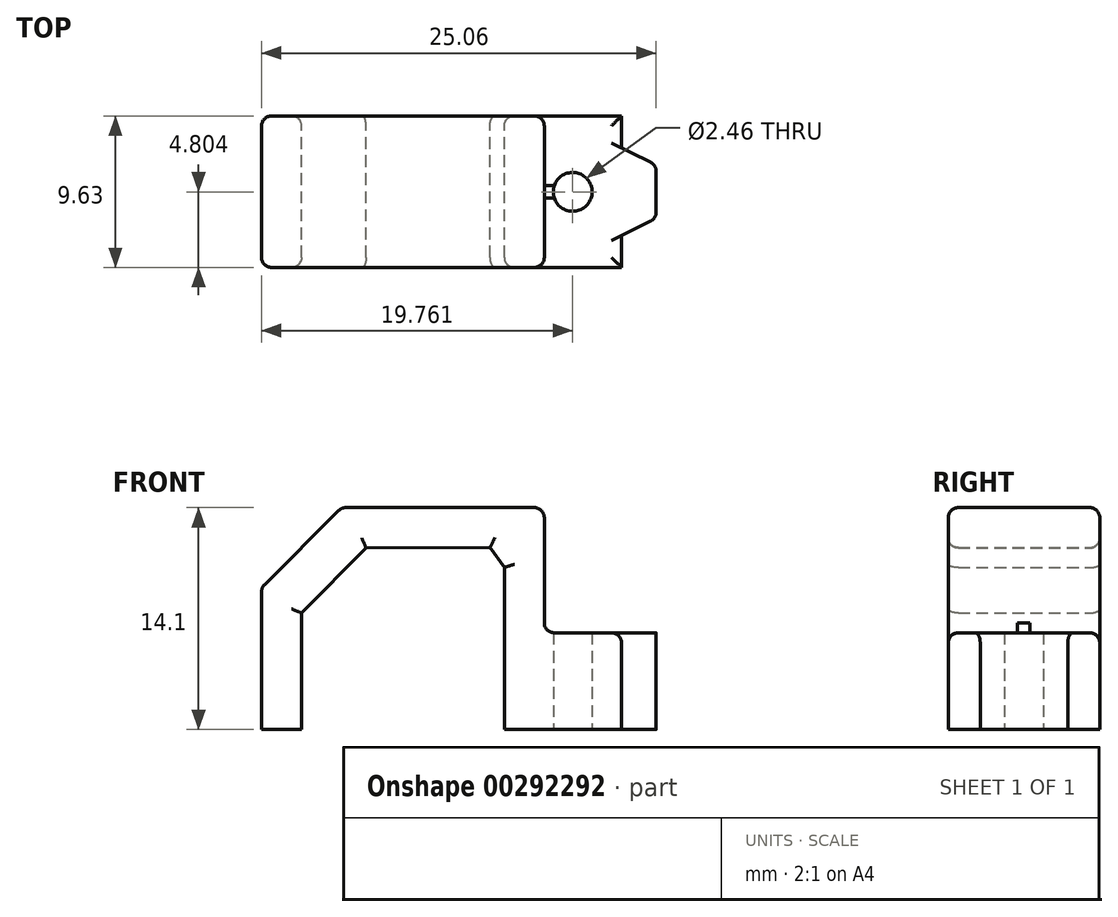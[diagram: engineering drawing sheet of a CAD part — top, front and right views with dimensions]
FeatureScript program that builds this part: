
annotation { "Feature Type Name" : "Feature", "Feature Type Description" : "" }
export const myFeature = defineFeature(function(context is Context, id is Id, definition is map)
    precondition{}
    {
        {
            var Q0;
            Q0=qCreatedBy(makeId("Front.planeOp"),FACE);
            var sketch = newSketch(context, id + "F0", { "sketchPlane" : qUnion([Q0])});
            skLineSegment(sketch, "E0", {"start": v(0, 0) * mm, "end": v(0, 6.14) * mm});
            skLineSegment(sketch, "E1", {"start": v(0, 6.14) * mm, "end": v(-4.9, 6.14) * mm});
            skLineSegment(sketch, "E2", {"start": v(-4.9, 6.14) * mm, "end": v(-4.9, 14.1) * mm});
            skLineSegment(sketch, "E3", {"start": v(-22.86, 0) * mm, "end": v(-20.32, 0) * mm});
            skLineSegment(sketch, "E4", {"start": v(-20.32, 0) * mm, "end": v(-20.32, 7.4) * mm});
            skLineSegment(sketch, "E5", {"start": v(-16.22, 11.53) * mm, "end": v(-8.35, 11.56) * mm});
            skLineSegment(sketch, "E6", {"start": v(-7.44, 10.3) * mm, "end": v(-7.44, 0) * mm});
            skLineSegment(sketch, "E7", {"start": v(-7.44, 0) * mm, "end": v(0, 0) * mm});
            skLineSegment(sketch, "E8", {"start": v(-7.44, 10.3) * mm, "end": v(-8.35, 11.56) * mm});
            skLineSegment(sketch, "E9", {"start": v(-17.78, 14.1) * mm, "end": v(-22.86, 9.02) * mm});
            skLineSegment(sketch, "E10", {"start": v(-16.22, 11.53) * mm, "end": v(-20.32, 7.4) * mm});
            skLineSegment(sketch, "E11", {"start": v(-22.86, 9.02) * mm, "end": v(-22.86, 0) * mm});
            skLineSegment(sketch, "E12", {"start": v(-17.78, 14.1) * mm, "end": v(-4.9, 14.1) * mm});
            skSolve(sketch);
        }
        {
            var Q0;
            Q0 = qSketchRegion(id + "F0", true);
            extrude(context, id + "F1", {"entities" : qUnion([Q0]), "depth" : 9.63 * mm});
        }
        {
            var Q0;
            Q0=makeQuery(id+"F1.opExtrude","SWEPT_FACE",FACE,{"disambiguationData":[OSD([sQuery(id+"F0.wireOp",EDGE,"E7")])]});
            var sketch = newSketch(context, id + "F2", { "sketchPlane" : qUnion([Q0])});
            skCircle(sketch, "E13", {"center": v(-3.1, 4.83) * mm, "radius": 1.17 * mm});
            skSolve(sketch);
        }
        {
            var Q0;
            Q0=sQuery(id+"F2.wireOp",VERTEX,"E13.center");
            var Q1;
            Q1=makeQuery(id+"F1.opExtrude","SWEPT_BODY",BODY,{"disambiguationData":[OSD([sQuery(id+"F0.wireOp",EDGE,"E0"),sQuery(id+"F0.wireOp",EDGE,"E1"),sQuery(id+"F0.wireOp",EDGE,"E2"),sQuery(id+"F0.wireOp",EDGE,"v06fyoa2-H6hD-baKa-V2WD-RjBCcUJbtUPS"),sQuery(id+"F0.wireOp",EDGE,"YEdOTz9l-d9wv-5XqQ-HbdA-mJVCXZZWVET7"),sQuery(id+"F0.wireOp",EDGE,"E3"),sQuery(id+"F0.wireOp",EDGE,"E4"),sQuery(id+"F0.wireOp",EDGE,"pneGorh0-Tr08-eoOQ-M8Zm-cxjPOqV0gIkG"),sQuery(id+"F0.wireOp",EDGE,"E5"),sQuery(id+"F0.wireOp",EDGE,"E6"),sQuery(id+"F0.wireOp",EDGE,"E7"),sQuery(id+"F0.wireOp",EDGE,"E8")])]});
            hole(context, id + "F3", {"style" : HoleStyle.SIMPLE, "endStyle" : HoleEndStyle.THROUGH, "holeDiameter" : 2.46 * mm, "tappedDepth" : 12.7 * mm, "tapClearance" : 3, "locations" : qUnion([Q0]), "scope" : qUnion([Q1])});
        }
        {
            var Q0;
            Q0=qCreatedBy(makeId("Top.planeOp"),FACE);
            var sketch = newSketch(context, id + "F4", { "sketchPlane" : qUnion([Q0])});
            skLineSegment(sketch, "E14", {"start": v(0, -7.6) * mm, "end": v(2.2, -6.5) * mm});
            skLineSegment(sketch, "E15", {"start": v(2.2, -3.12) * mm, "end": v(0, -2.03) * mm});
            skLineSegment(sketch, "E16", {"start": v(2.2, -6.5) * mm, "end": v(2.2, -3.12) * mm});
            skLineSegment(sketch, "E17", {"start": v(0, -7.6) * mm, "end": v(0, -2.03) * mm});
            skSolve(sketch);
        }
        {
            var Q0;
            Q0=makeQuery(id+"F4.imprint","IMPRINT",FACE,{"disambiguationData":[TD([[makeQuery(id+"F4.imprint","IMPRINT",EDGE,{"derivedFrom":sQuery(id+"F4.wireOp",EDGE,"E14")}),1.0]])]});
            var Q1;
            Q1=makeQuery(id+"F1.opExtrude","SWEPT_FACE",FACE,{"disambiguationData":[OSD([sQuery(id+"F0.wireOp",EDGE,"E1")])]});
            extrude(context, id + "F5", {"entities" : qUnion([Q0]), "operationType" : NewBodyOperationType.ADD, "endBound" : BoundingType.UP_TO_SURFACE, "endBoundEntityFace" : qUnion([Q1]), "depth" : 6.22 * mm});
        }
        {
            var Q0;
            Q0=makeQuery(id+"F1.opExtrude","CAP_EDGE",EDGE,{"disambiguationData":[OSD([sQuery(id+"F0.wireOp",EDGE,"v06fyoa2-H6hD-baKa-V2WD-RjBCcUJbtUPS")])],"isStart":true});
            var Q1;
            Q1=makeQuery(id+"F1.opExtrude","SWEPT_EDGE",EDGE,{"disambiguationData":[OSD([sQuery(id+"F0.wireOp",EDGE,"v06fyoa2-H6hD-baKa-V2WD-RjBCcUJbtUPS"),sQuery(id+"F0.wireOp",EDGE,"YEdOTz9l-d9wv-5XqQ-HbdA-mJVCXZZWVET7")])]});
            var Q2;
            Q2=makeQuery(id+"F1.opExtrude","CAP_EDGE",EDGE,{"disambiguationData":[OSD([sQuery(id+"F0.wireOp",EDGE,"v06fyoa2-H6hD-baKa-V2WD-RjBCcUJbtUPS")])],"isStart":false});
            var Q3;
            Q3=makeQuery(id+"F1.opExtrude","SWEPT_EDGE",EDGE,{"disambiguationData":[OSD([sQuery(id+"F0.wireOp",EDGE,"E2"),sQuery(id+"F0.wireOp",EDGE,"v06fyoa2-H6hD-baKa-V2WD-RjBCcUJbtUPS")])]});
            var Q4;
            Q4=makeQuery(id+"F1.opExtrude","CAP_EDGE",EDGE,{"disambiguationData":[OSD([sQuery(id+"F0.wireOp",EDGE,"E6")])],"isStart":true});
            var Q5;
            Q5=makeQuery(id+"F1.opExtrude","CAP_EDGE",EDGE,{"disambiguationData":[OSD([sQuery(id+"F0.wireOp",EDGE,"E8")])],"isStart":true});
            var Q6;
            Q6=makeQuery(id+"F1.opExtrude","CAP_EDGE",EDGE,{"disambiguationData":[OSD([sQuery(id+"F0.wireOp",EDGE,"E5")])],"isStart":true});
            var Q7;
            Q7=makeQuery(id+"F1.opExtrude","CAP_EDGE",EDGE,{"disambiguationData":[OSD([sQuery(id+"F0.wireOp",EDGE,"pneGorh0-Tr08-eoOQ-M8Zm-cxjPOqV0gIkG")])],"isStart":true});
            var Q8;
            Q8=makeQuery(id+"F1.opExtrude","CAP_EDGE",EDGE,{"disambiguationData":[OSD([sQuery(id+"F0.wireOp",EDGE,"E4")])],"isStart":true});
            var Q9;
            Q9=makeQuery(id+"F1.opExtrude","CAP_EDGE",EDGE,{"disambiguationData":[OSD([sQuery(id+"F0.wireOp",EDGE,"YEdOTz9l-d9wv-5XqQ-HbdA-mJVCXZZWVET7")])],"isStart":true});
            var Q10;
            Q10=makeQuery(id+"F1.opExtrude","CAP_EDGE",EDGE,{"disambiguationData":[OSD([sQuery(id+"F0.wireOp",EDGE,"YEdOTz9l-d9wv-5XqQ-HbdA-mJVCXZZWVET7")])],"isStart":false});
            var Q11;
            Q11=makeQuery(id+"F1.opExtrude","CAP_EDGE",EDGE,{"disambiguationData":[OSD([sQuery(id+"F0.wireOp",EDGE,"E4")])],"isStart":false});
            var Q12;
            Q12=makeQuery(id+"F1.opExtrude","CAP_EDGE",EDGE,{"disambiguationData":[OSD([sQuery(id+"F0.wireOp",EDGE,"pneGorh0-Tr08-eoOQ-M8Zm-cxjPOqV0gIkG")])],"isStart":false});
            var Q13;
            Q13=makeQuery(id+"F1.opExtrude","CAP_EDGE",EDGE,{"disambiguationData":[OSD([sQuery(id+"F0.wireOp",EDGE,"E5")])],"isStart":false});
            var Q14;
            Q14=makeQuery(id+"F1.opExtrude","CAP_EDGE",EDGE,{"disambiguationData":[OSD([sQuery(id+"F0.wireOp",EDGE,"E8")])],"isStart":false});
            var Q15;
            Q15=makeQuery(id+"F1.opExtrude","CAP_EDGE",EDGE,{"disambiguationData":[OSD([sQuery(id+"F0.wireOp",EDGE,"E6")])],"isStart":false});
            var Q16;
            Q16=makeQuery(id+"F1.opExtrude","CAP_EDGE",EDGE,{"disambiguationData":[OSD([sQuery(id+"F0.wireOp",EDGE,"E2")])],"isStart":true});
            var Q17;
            Q17=makeQuery(id+"F1.opExtrude","CAP_EDGE",EDGE,{"disambiguationData":[OSD([sQuery(id+"F0.wireOp",EDGE,"E2")])],"isStart":false});
            var Q18;
            Q18=makeQuery(id+"F1.opExtrude","SWEPT_EDGE",EDGE,{"disambiguationData":[OSD([sQuery(id+"F0.wireOp",EDGE,"E0"),sQuery(id+"F0.wireOp",EDGE,"E1")])]});
            var Q19;
            Q19=makeQuery(id+"F1.opExtrude","CAP_EDGE",EDGE,{"disambiguationData":[OSD([sQuery(id+"F0.wireOp",EDGE,"E1")])],"isStart":true});
            var Q20;
            Q20=makeQuery(id+"F1.opExtrude","CAP_EDGE",EDGE,{"disambiguationData":[OSD([sQuery(id+"F0.wireOp",EDGE,"E1")])],"isStart":false});
            var Q21;
            Q21=makeQuery(id+"F1.opExtrude","CAP_EDGE",EDGE,{"disambiguationData":[OSD([sQuery(id+"F0.wireOp",EDGE,"E9")])],"isStart":false});
            var Q22;
            Q22=makeQuery(id+"F1.opExtrude","CAP_EDGE",EDGE,{"disambiguationData":[OSD([sQuery(id+"F0.wireOp",EDGE,"E11")])],"isStart":false});
            var Q23;
            Q23=makeQuery(id+"F1.opExtrude","CAP_EDGE",EDGE,{"disambiguationData":[OSD([sQuery(id+"F0.wireOp",EDGE,"E10")])],"isStart":false});
            var Q24;
            Q24=makeQuery(id+"F1.opExtrude","CAP_EDGE",EDGE,{"disambiguationData":[OSD([sQuery(id+"F0.wireOp",EDGE,"E9")])],"isStart":true});
            var Q25;
            Q25=makeQuery(id+"F1.opExtrude","CAP_EDGE",EDGE,{"disambiguationData":[OSD([sQuery(id+"F0.wireOp",EDGE,"E11")])],"isStart":true});
            var Q26;
            Q26=makeQuery(id+"F1.opExtrude","CAP_EDGE",EDGE,{"disambiguationData":[OSD([sQuery(id+"F0.wireOp",EDGE,"E10")])],"isStart":true});
            var Q27;
            Q27=makeQuery(id+"F1.opExtrude","CAP_EDGE",EDGE,{"disambiguationData":[OSD([sQuery(id+"F0.wireOp",EDGE,"E12")])],"isStart":true});
            var Q28;
            Q28=makeQuery(id+"F1.opExtrude","CAP_EDGE",EDGE,{"disambiguationData":[OSD([sQuery(id+"F0.wireOp",EDGE,"E12")])],"isStart":false});
            var Q29;
            Q29=makeQuery(id+"F1.opExtrude","SWEPT_EDGE",EDGE,{"disambiguationData":[OSD([sQuery(id+"F0.wireOp",EDGE,"E9"),sQuery(id+"F0.wireOp",EDGE,"E12")])]});
            var Q30;
            Q30=makeQuery(id+"F1.opExtrude","SWEPT_EDGE",EDGE,{"disambiguationData":[OSD([sQuery(id+"F0.wireOp",EDGE,"E9"),sQuery(id+"F0.wireOp",EDGE,"E11")])]});
            var Q31;
            Q31=makeQuery(id+"F5.opExtrude","TWEAK_EDGE",EDGE,{"derivedFrom":[makeQuery(id+"F1.opExtrude","SWEPT_FACE",FACE,{"disambiguationData":[OSD([sQuery(id+"F0.wireOp",EDGE,"E1")])]}),makeQuery(id+"F4.imprint","IMPRINT",EDGE,{"derivedFrom":sQuery(id+"F4.wireOp",EDGE,"E14")})]});
            var Q32;
            Q32=makeQuery(id+"F5.opExtrude","TWEAK_EDGE",EDGE,{"derivedFrom":[makeQuery(id+"F1.opExtrude","SWEPT_FACE",FACE,{"disambiguationData":[OSD([sQuery(id+"F0.wireOp",EDGE,"E1")])]}),makeQuery(id+"F4.imprint","IMPRINT",EDGE,{"derivedFrom":sQuery(id+"F4.wireOp",EDGE,"E16")})]});
            var Q33;
            Q33=makeQuery(id+"F5.opExtrude","TWEAK_EDGE",EDGE,{"derivedFrom":[makeQuery(id+"F1.opExtrude","SWEPT_FACE",FACE,{"disambiguationData":[OSD([sQuery(id+"F0.wireOp",EDGE,"E1")])]}),makeQuery(id+"F4.imprint","IMPRINT",EDGE,{"derivedFrom":sQuery(id+"F4.wireOp",EDGE,"E15")})]});
            var Q34;
            Q34=makeQuery(id+"F5.opExtrude","SWEPT_EDGE",EDGE,{"disambiguationData":[OSD([sQuery(id+"F4.wireOp",EDGE,"E14"),sQuery(id+"F4.wireOp",EDGE,"E16")])]});
            var Q35;
            Q35=makeQuery(id+"F5.opExtrude","SWEPT_EDGE",EDGE,{"disambiguationData":[OSD([sQuery(id+"F4.wireOp",EDGE,"E15"),sQuery(id+"F4.wireOp",EDGE,"E16")])]});
            fillet(context, id + "F6", {"entities" : qUnion([Q0, Q1, Q2, Q3, Q4, Q5, Q6, Q7, Q8, Q9, Q10, Q11, Q12, Q13, Q14, Q15, Q16, Q17, Q18, Q19, Q20, Q21, Q22, Q23, Q24, Q25, Q26, Q27, Q28, Q29, Q30, Q31, Q32, Q33, Q34, Q35]), "radius" : 0.64 * mm, "allowEdgeOverflow" : false});
        }
    });
